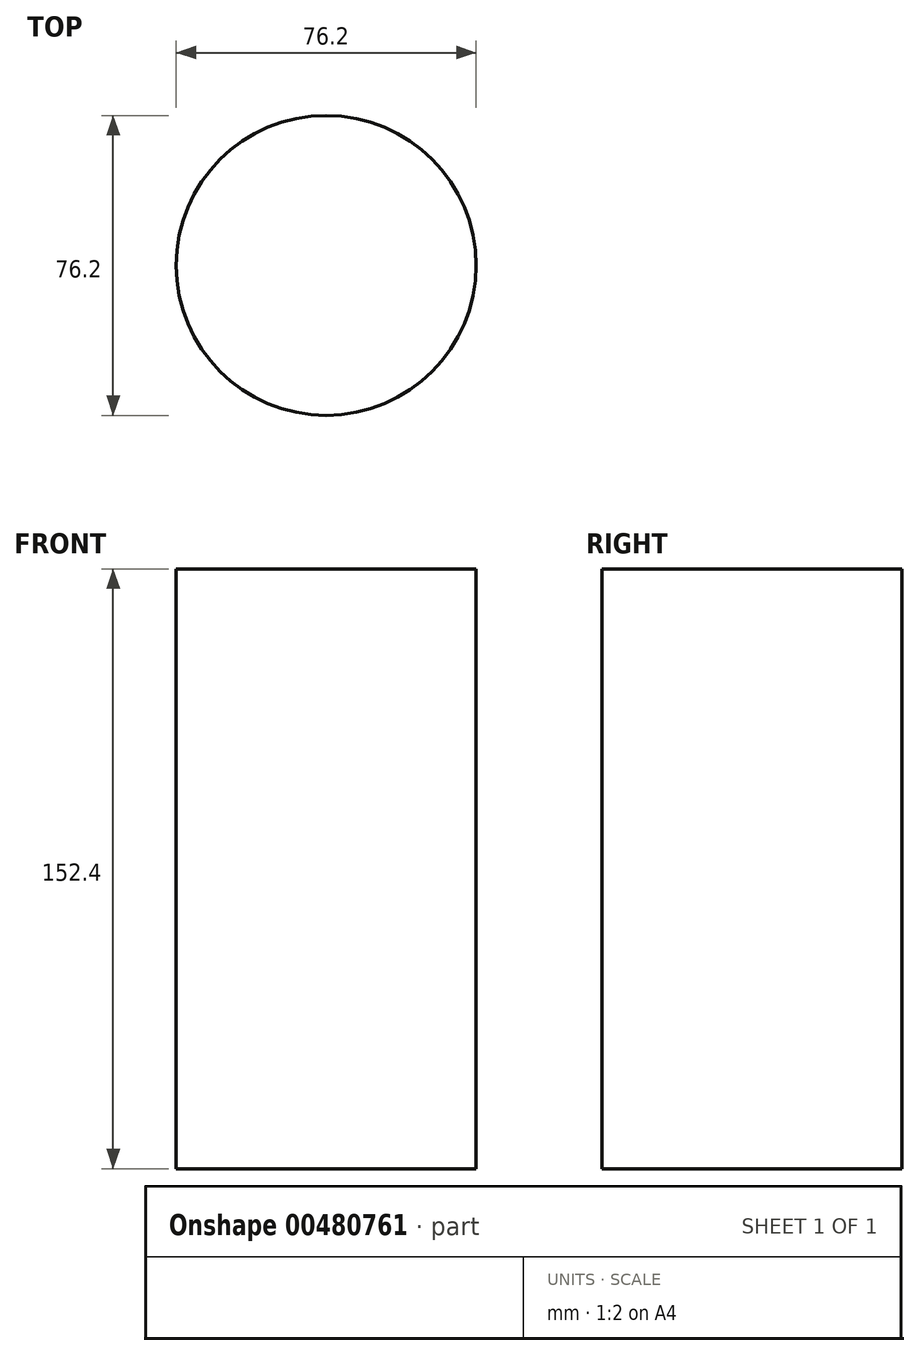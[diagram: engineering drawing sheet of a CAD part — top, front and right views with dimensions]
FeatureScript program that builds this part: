
annotation { "Feature Type Name" : "Feature", "Feature Type Description" : "" }
export const myFeature = defineFeature(function(context is Context, id is Id, definition is map)
    precondition{}
    {
        {
            var Q0;
            Q0=qCreatedBy(makeId("Top.planeOp"),FACE);
            var sketch = newSketch(context, id + "F0", { "sketchPlane" : qUnion([Q0])});
            skCircle(sketch, "E0", {"center": v(0, 0) * mm, "radius": 38.1 * mm});
            skSolve(sketch);
        }
        {
            var Q0;
            Q0=makeQuery(id+"F0.imprint","IMPRINT",FACE,{"disambiguationData":[TD([[makeQuery(id+"F0.imprint","IMPRINT",EDGE,{"derivedFrom":sQuery(id+"F0.wireOp",EDGE,"E0")}),1.0]])]});
            extrude(context, id + "F1", {"entities" : qUnion([Q0]), "depth" : 152.4 * mm});
        }
    });
